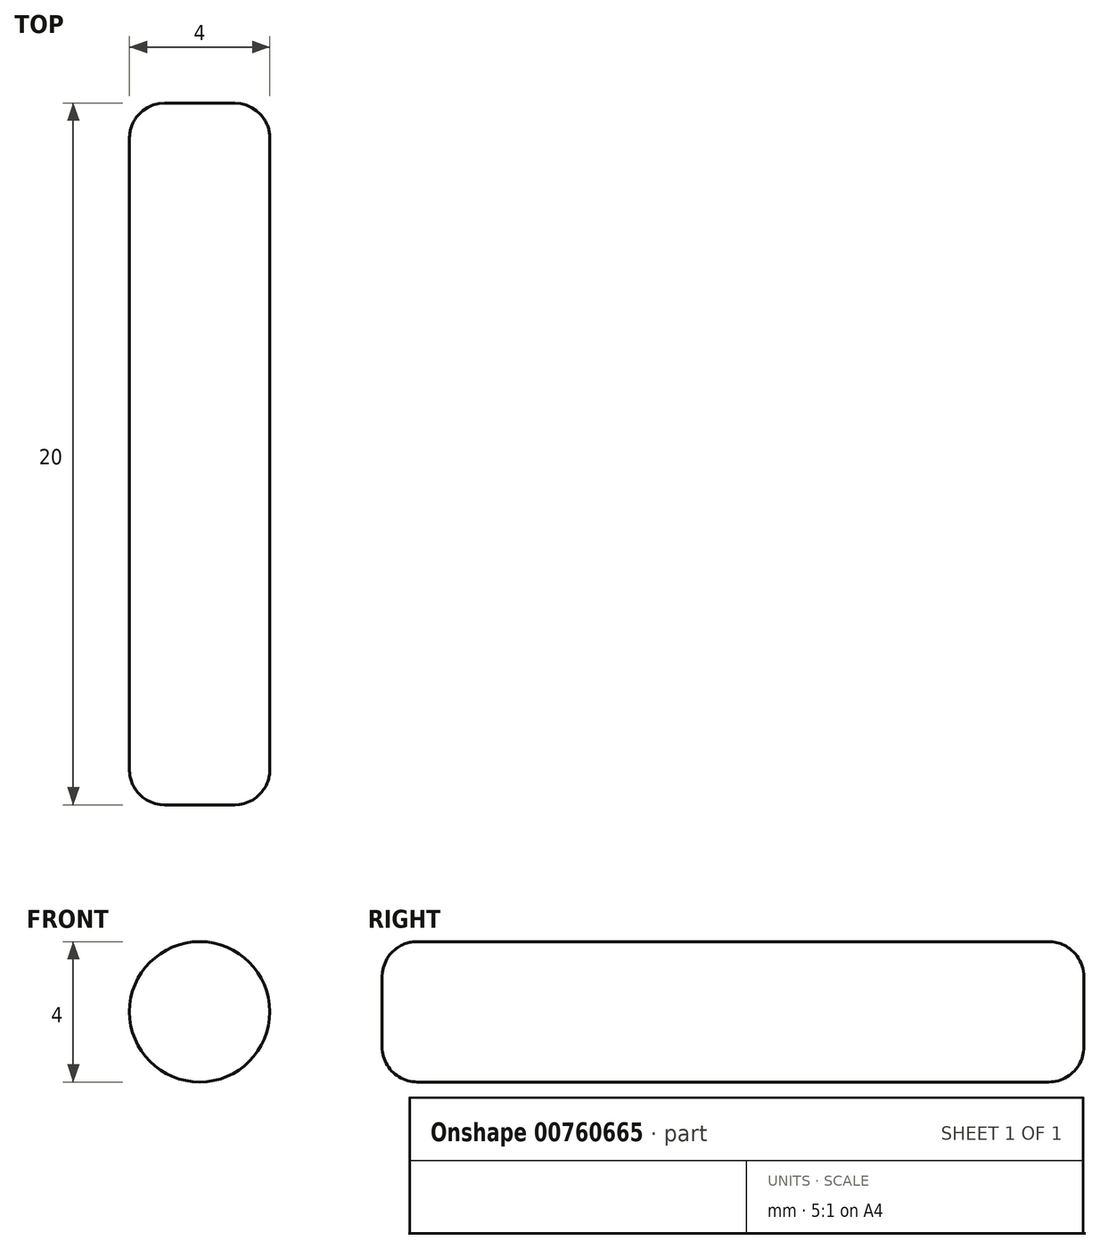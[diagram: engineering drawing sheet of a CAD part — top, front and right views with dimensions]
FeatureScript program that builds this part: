
annotation { "Feature Type Name" : "Feature", "Feature Type Description" : "" }
export const myFeature = defineFeature(function(context is Context, id is Id, definition is map)
    precondition{}
    {
        {
            var Q0;
            Q0=qCreatedBy(makeId("Front.planeOp"),FACE);
            var sketch = newSketch(context, id + "F0", { "sketchPlane" : qUnion([Q0])});
            skCircle(sketch, "E0", {"center": v(0, 0) * mm, "radius": 2 * mm});
            skSolve(sketch);
        }
        {
            var Q0;
            Q0 = qSketchRegion(id + "F0", true);
            extrude(context, id + "F1", {"entities" : qUnion([Q0]), "endBound" : BoundingType.SYMMETRIC, "depth" : 20 * mm, "offsetDistance" : 25 * mm});
        }
        {
            var Q0;
            Q0=makeQuery(id+"F1.opExtrude","CAP_EDGE",EDGE,{"disambiguationData":[OSD([sQuery(id+"F0.wireOp",EDGE,"E0")])],"isStart":true});
            var Q1;
            Q1=makeQuery(id+"F1.opExtrude","CAP_EDGE",EDGE,{"disambiguationData":[OSD([sQuery(id+"F0.wireOp",EDGE,"E0")])],"isStart":false});
            fillet(context, id + "F2", {"entities" : qUnion([Q0, Q1]), "radius" : 1 * mm, "tangentPropagation" : true, "allowEdgeOverflow" : false});
        }
    });
